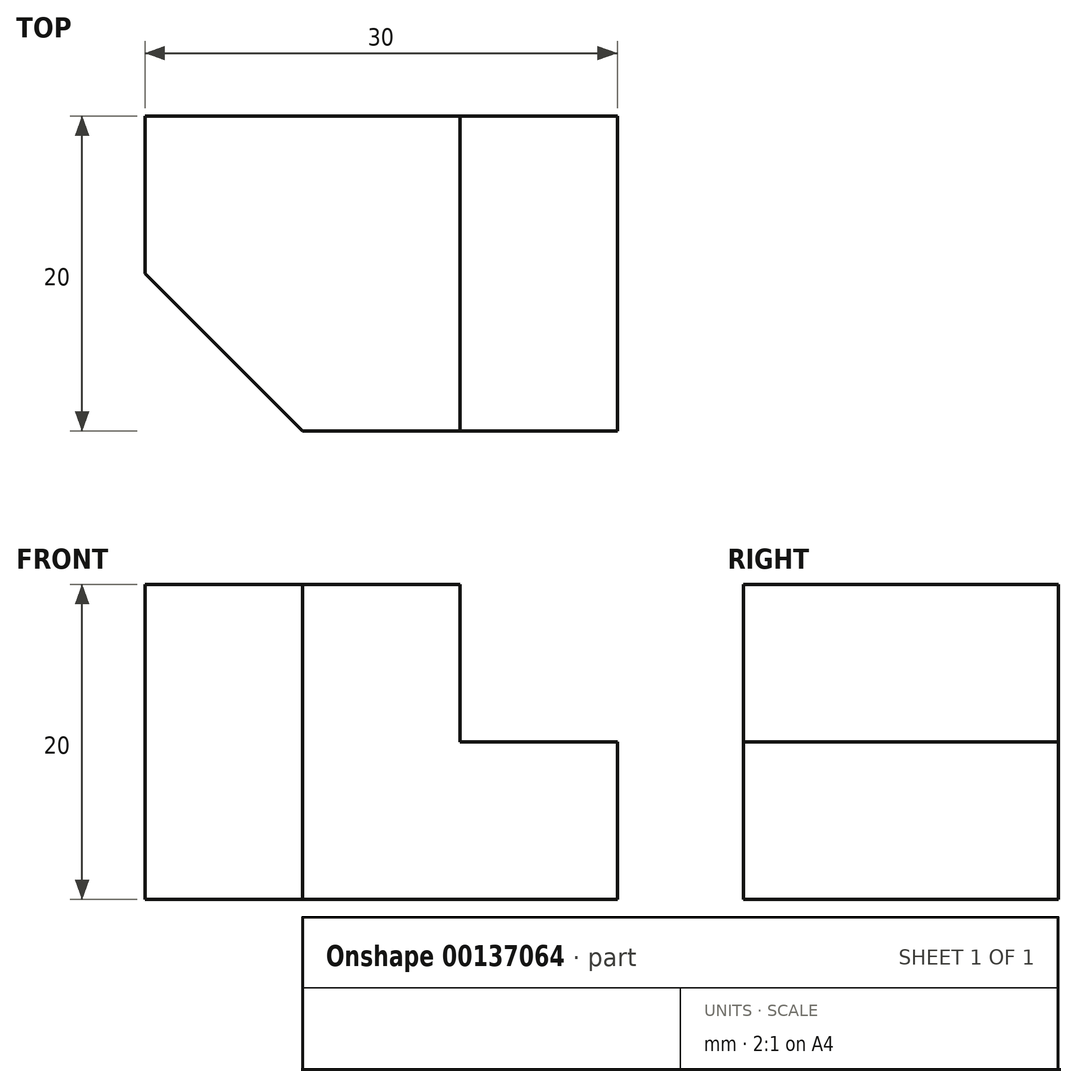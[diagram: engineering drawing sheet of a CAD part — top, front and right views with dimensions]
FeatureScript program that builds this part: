
annotation { "Feature Type Name" : "Feature", "Feature Type Description" : "" }
export const myFeature = defineFeature(function(context is Context, id is Id, definition is map)
    precondition{}
    {
        {
            var Q0;
            Q0=qCreatedBy(makeId("Front.planeOp"),FACE);
            var sketch = newSketch(context, id + "F0", { "sketchPlane" : qUnion([Q0])});
            skLineSegment(sketch, "E0", {"start": v(0, 0) * mm, "end": v(30, 0) * mm});
            skLineSegment(sketch, "E1", {"start": v(30, 0) * mm, "end": v(30, 10) * mm});
            skLineSegment(sketch, "E2", {"start": v(30, 10) * mm, "end": v(20, 10) * mm});
            skLineSegment(sketch, "E3", {"start": v(20, 10) * mm, "end": v(20, 20) * mm});
            skLineSegment(sketch, "E4", {"start": v(20, 20) * mm, "end": v(0, 20) * mm});
            skLineSegment(sketch, "E5", {"start": v(0, 20) * mm, "end": v(0, 0) * mm});
            skSolve(sketch);
        }
        {
            var Q0;
            Q0 = qSketchRegion(id + "F0", true);
            extrude(context, id + "F1", {"entities" : qUnion([Q0]), "oppositeDirection" : true, "depth" : 20 * mm});
        }
        {
            var Q0;
            Q0=makeQuery(id+"F1.opExtrude","SWEPT_FACE",FACE,{"disambiguationData":[OSD([sQuery(id+"F0.wireOp",EDGE,"E4")])]});
            var sketch = newSketch(context, id + "F2", { "sketchPlane" : qUnion([Q0])});
            skLineSegment(sketch, "E6", {"start": v(0, 10) * mm, "end": v(10, 0) * mm});
            skLineSegment(sketch, "E7", {"start": v(10, 0) * mm, "end": v(0, 0) * mm});
            skLineSegment(sketch, "E8", {"start": v(0, 0) * mm, "end": v(0, 10) * mm});
            skSolve(sketch);
        }
        {
            var Q0;
            Q0 = qSketchRegion(id + "F2", true);
            extrude(context, id + "F3", {"entities" : qUnion([Q0]), "operationType" : NewBodyOperationType.REMOVE, "endBound" : BoundingType.THROUGH_ALL, "oppositeDirection" : true, "depth" : 25 * mm});
        }
    });
